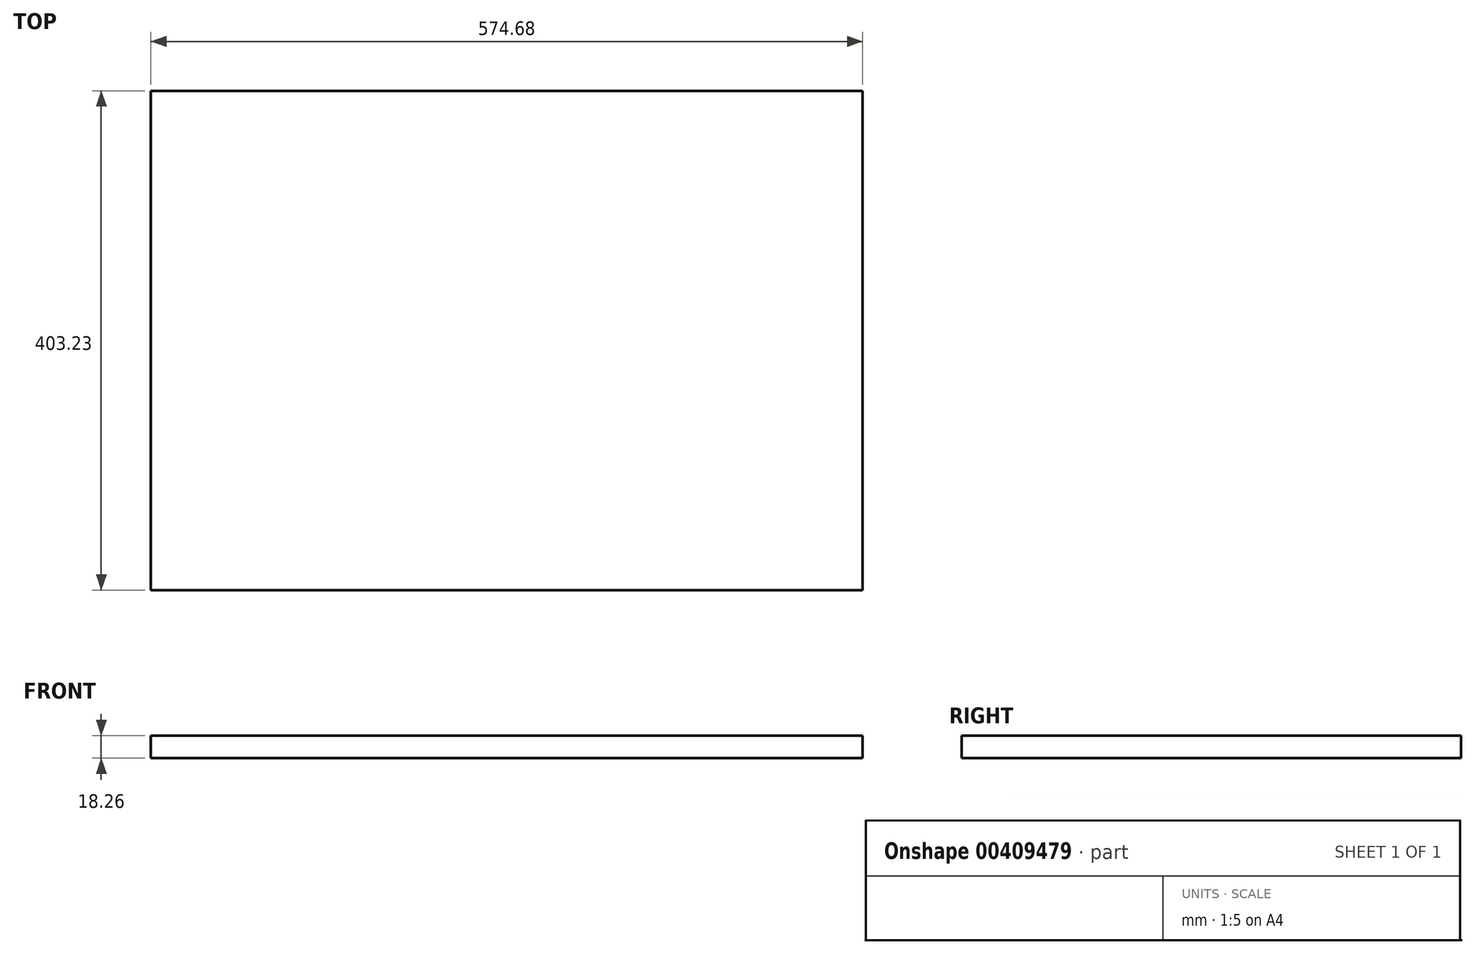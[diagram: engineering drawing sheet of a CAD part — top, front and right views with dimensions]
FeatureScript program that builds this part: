
annotation { "Feature Type Name" : "Feature", "Feature Type Description" : "" }
export const myFeature = defineFeature(function(context is Context, id is Id, definition is map)
    precondition{}
    {
        {
            var Q0;
            Q0=qCreatedBy(makeId("Front.planeOp"),FACE);
            var sketch = newSketch(context, id + "F0", { "sketchPlane" : qUnion([Q0])});
            skLineSegment(sketch, "E0.bottom", {"start": v(0, 0) * mm, "end": v(574.68, 0) * mm});
            skLineSegment(sketch, "E0.top", {"start": v(0, 18.26) * mm, "end": v(574.68, 18.26) * mm});
            skLineSegment(sketch, "E0.left", {"start": v(0, 0) * mm, "end": v(0, 18.26) * mm});
            skLineSegment(sketch, "E0.right", {"start": v(574.68, 0) * mm, "end": v(574.68, 18.26) * mm});
            skSolve(sketch);
        }
        {
            var Q0;
            Q0=makeQuery(id+"F0.imprint","IMPRINT",FACE,{"disambiguationData":[TD([[makeQuery(id+"F0.imprint","IMPRINT",EDGE,{"derivedFrom":sQuery(id+"F0.wireOp",EDGE,"E0.bottom")}),1.0]])]});
            extrude(context, id + "F1", {"entities" : qUnion([Q0]), "depth" : 403.22 * mm});
        }
    });
